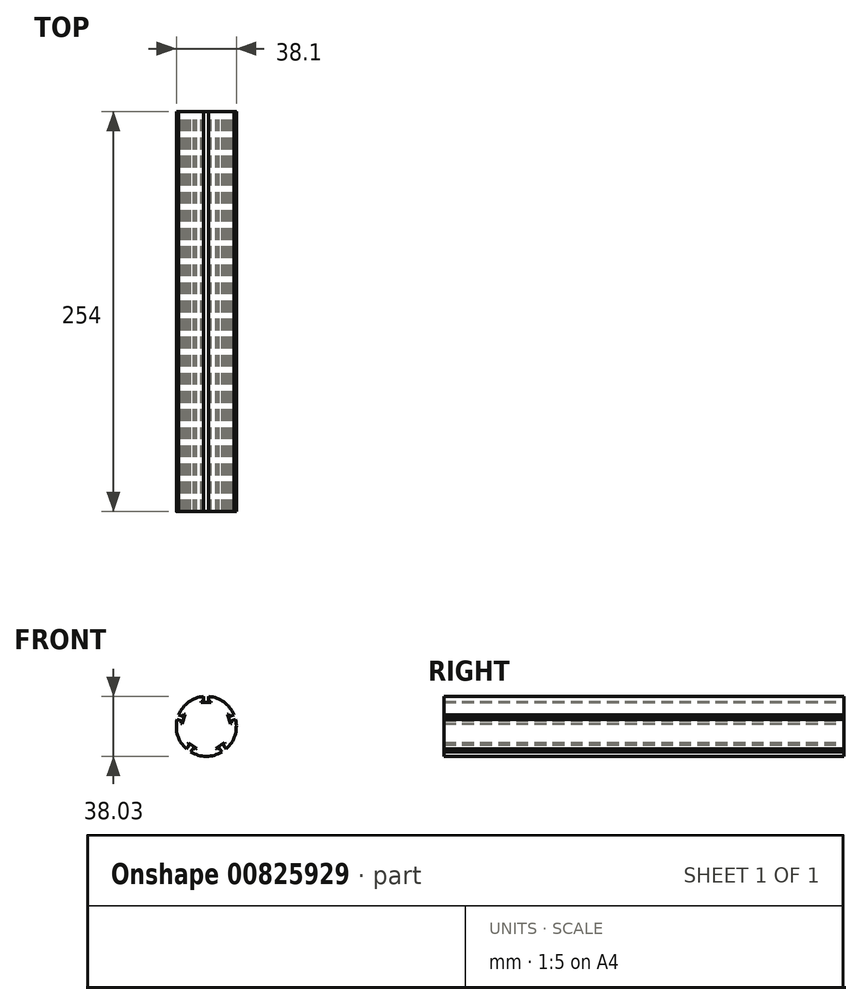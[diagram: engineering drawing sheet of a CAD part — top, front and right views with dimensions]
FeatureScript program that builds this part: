
annotation { "Feature Type Name" : "Feature", "Feature Type Description" : "" }
export const myFeature = defineFeature(function(context is Context, id is Id, definition is map)
    precondition{}
    {
        {
            var Q0;
            Q0=qCreatedBy(makeId("Front.planeOp"),FACE);
            var sketch = newSketch(context, id + "F0", { "sketchPlane" : qUnion([Q0])});
            skCircle(sketch, "E0", {"center": v(0, 0) * mm, "radius": 19.05 * mm});
            skLineSegment(sketch, "E1", {"start": v(0, 19.05) * mm, "end": v(0, -19.05) * mm});
            skLineSegment(sketch, "E2", {"start": v(-19.05, 0) * mm, "end": v(19.05, 0) * mm});
            skSolve(sketch);
        }
        {
            var Q0;
            Q0=makeQuery(id+"F0.imprint","IMPRINT",FACE,{"disambiguationData":[TD([[makeQuery(id+"F0.imprint","IMPRINT",EDGE,{"derivedFrom":sQuery(id+"F0.wireOp",EDGE,"E0")}),1.0]])]});
            extrude(context, id + "F1", {"entities" : qUnion([Q0]), "depth" : 254 * mm, "offsetDistance" : 25.4 * mm});
        }
        {
            var Q0;
            Q0=makeQuery(id+"F1.opExtrude","CAP_FACE",FACE,{"disambiguationData":[OSD([sQuery(id+"F0.wireOp",EDGE,"E0")])],"isStart":true});
            var Q1;
            Q1=makeQuery(id+"F1.opExtrude","CAP_FACE",FACE,{"disambiguationData":[OSD([sQuery(id+"F0.wireOp",EDGE,"E0")])],"isStart":false});
            cPlane(context, id + "F2", {"entities" : qUnion([Q0, Q1]), "cplaneType" : CPlaneType.MID_PLANE, "offset" : 50.8 * mm, "oppositeDirection" : true, "width" : 152.4 * mm, "height" : 152.4 * mm});
        }
        {
            var Q0;
            Q0=qCreatedBy(id+"F2.planeOp",FACE);
            var sketch = newSketch(context, id + "F3", { "sketchPlane" : qUnion([Q0])});
            skLineSegment(sketch, "E3", {"start": v(0, 19.08) * mm, "end": v(0, 0) * mm});
            skSolve(sketch);
        }
        {
            var Q0;
            Q0=makeQuery(id+"F1.opExtrude","CAP_FACE",FACE,{"disambiguationData":[OSD([sQuery(id+"F0.wireOp",EDGE,"E0")])],"isStart":true});
            var sketch = newSketch(context, id + "F4", { "sketchPlane" : qUnion([Q0])});
            skLineSegment(sketch, "E4.left", {"start": v(-3.16, 15.9) * mm, "end": v(-3.16, 15.1) * mm});
            skLineSegment(sketch, "E4.right", {"start": v(3.2, 15.9) * mm, "end": v(3.2, 15.1) * mm});
            skLineSegment(sketch, "E5.bottom", {"start": v(-3.16, 15.9) * mm, "end": v(3.2, 15.9) * mm});
            skLineSegment(sketch, "E5.top", {"start": v(-3.16, 15.1) * mm, "end": v(3.2, 15.1) * mm});
            skLineSegment(sketch, "E6.bottom", {"start": v(-1.59, 15.27) * mm, "end": v(1.59, 15.27) * mm});
            skLineSegment(sketch, "E6.top", {"start": v(-1.59, 20.27) * mm, "end": v(1.59, 20.27) * mm});
            skLineSegment(sketch, "E6.left", {"start": v(-1.59, 15.27) * mm, "end": v(-1.59, 20.27) * mm});
            skLineSegment(sketch, "E6.right", {"start": v(1.59, 15.27) * mm, "end": v(1.59, 20.27) * mm});
            skLineSegment(sketch, "E7", {"start": v(-1.59, 15.27) * mm, "end": v(1.59, 20.27) * mm, "construction": true});
            skLineSegment(sketch, "E8", {"start": v(0, 17.77) * mm, "end": v(0, 20.27) * mm, "construction": true});
            skSolve(sketch);
        }
        {
            var Q0;
            {var subQ0=sQuery(id+"F4.wireOp",EDGE,"E4.left");Q0=makeQuery(id+"F4.imprint","IMPRINT",FACE,{"disambiguationData":[TD([[makeQuery(id+"F4.imprint","IMPRINT",EDGE,{"derivedFrom":subQ0}),1.0]])]});}
            var Q1;
            {var subQ5=sQuery(id+"F4.wireOp",EDGE,"E6.bottom");Q1=makeQuery(id+"F4.imprint","IMPRINT",FACE,{"disambiguationData":[TD([[makeQuery(id+"F4.imprint","IMPRINT",EDGE,{"derivedFrom":subQ5}),1.0]])]});}
            var Q2;
            {var subQ0=sQuery(id+"F4.wireOp",EDGE,"E4.right");Q2=makeQuery(id+"F4.imprint","IMPRINT",FACE,{"disambiguationData":[TD([[makeQuery(id+"F4.imprint","IMPRINT",EDGE,{"derivedFrom":subQ0}),-1.0]])]});}
            var Q3;
            {var subQ0=sQuery(id+"F4.wireOp",EDGE,"E6.left");var subQ1=sQuery(id+"F4.wireOp",EDGE,"E5.bottom");var subQ2=makeQuery(id+"F4.imprint","INTERSECT",VERTEX,{"derivedFrom":[subQ1,subQ0]});Q3=makeQuery(id+"F4.imprint","IMPRINT",FACE,{"disambiguationData":[TD([[makeQuery(id+"F4.imprint","IMPRINT",EDGE,{"disambiguationData":[TD([[subQ2,-1.0]])],"derivedFrom":subQ1}),1.0]])]});}
            var Q4;
            {var subQ0=sQuery(id+"F4.wireOp",EDGE,"E6.top");Q4=makeQuery(id+"F4.imprint","IMPRINT",FACE,{"disambiguationData":[TD([[makeQuery(id+"F4.imprint","IMPRINT",EDGE,{"derivedFrom":subQ0}),-1.0]])]});}
            extrude(context, id + "F5", {"entities" : qUnion([Q0, Q1, Q2, Q3, Q4]), "endBound" : BoundingType.THROUGH_ALL, "oppositeDirection" : true, "depth" : 25.4 * mm, "offsetDistance" : 25.4 * mm});
        }
        {
            var Q0;
            Q0=qCreatedBy(makeId("Right.planeOp"),FACE);
            var sketch = newSketch(context, id + "F6", { "sketchPlane" : qUnion([Q0])});
            skLineSegment(sketch, "E9", {"start": v(0, 0) * mm, "end": v(-126.05, 0) * mm});
            skSolve(sketch);
        }
        {
            var Q0;
            Q0=makeQuery(id+"F5.opExtrude","SWEPT_BODY",BODY,{"disambiguationData":[OSD([sQuery(id+"F4.wireOp",EDGE,"3gnbSLrJ-n7Bi-cuiK-82wk-3F1PXjoPZ2vk.bottom"),sQuery(id+"F4.wireOp",EDGE,"3gnbSLrJ-n7Bi-cuiK-82wk-3F1PXjoPZ2vk.top"),sQuery(id+"F4.wireOp",EDGE,"3gnbSLrJ-n7Bi-cuiK-82wk-3F1PXjoPZ2vk.left"),sQuery(id+"F4.wireOp",EDGE,"3gnbSLrJ-n7Bi-cuiK-82wk-3F1PXjoPZ2vk.right")])]});
            var Q1;
            Q1=makeQuery(id+"F5.opExtrude","SWEPT_BODY",BODY,{"disambiguationData":[OSD([sQuery(id+"F4.wireOp",EDGE,"E5.bottom"),sQuery(id+"F4.wireOp",EDGE,"E5.top"),sQuery(id+"F4.wireOp",EDGE,"E4.left"),sQuery(id+"F4.wireOp",EDGE,"E4.right"),sQuery(id+"F4.wireOp",EDGE,"E6.bottom"),sQuery(id+"F4.wireOp",EDGE,"E6.top"),sQuery(id+"F4.wireOp",EDGE,"E6.left"),sQuery(id+"F4.wireOp",EDGE,"E6.right")])]});
            var Q2;
            Q2=sQuery(id+"F6.wireOp",EDGE,"E9");
            circularPattern(context, id + "F7", {"operationType" : NewBodyOperationType.REMOVE, "entities" : qUnion([Q0, Q1]), "axis" : qUnion([Q2]), "angle" : 360 * degree, "instanceCount" : 5, "equalSpace" : true});
        }
    });
